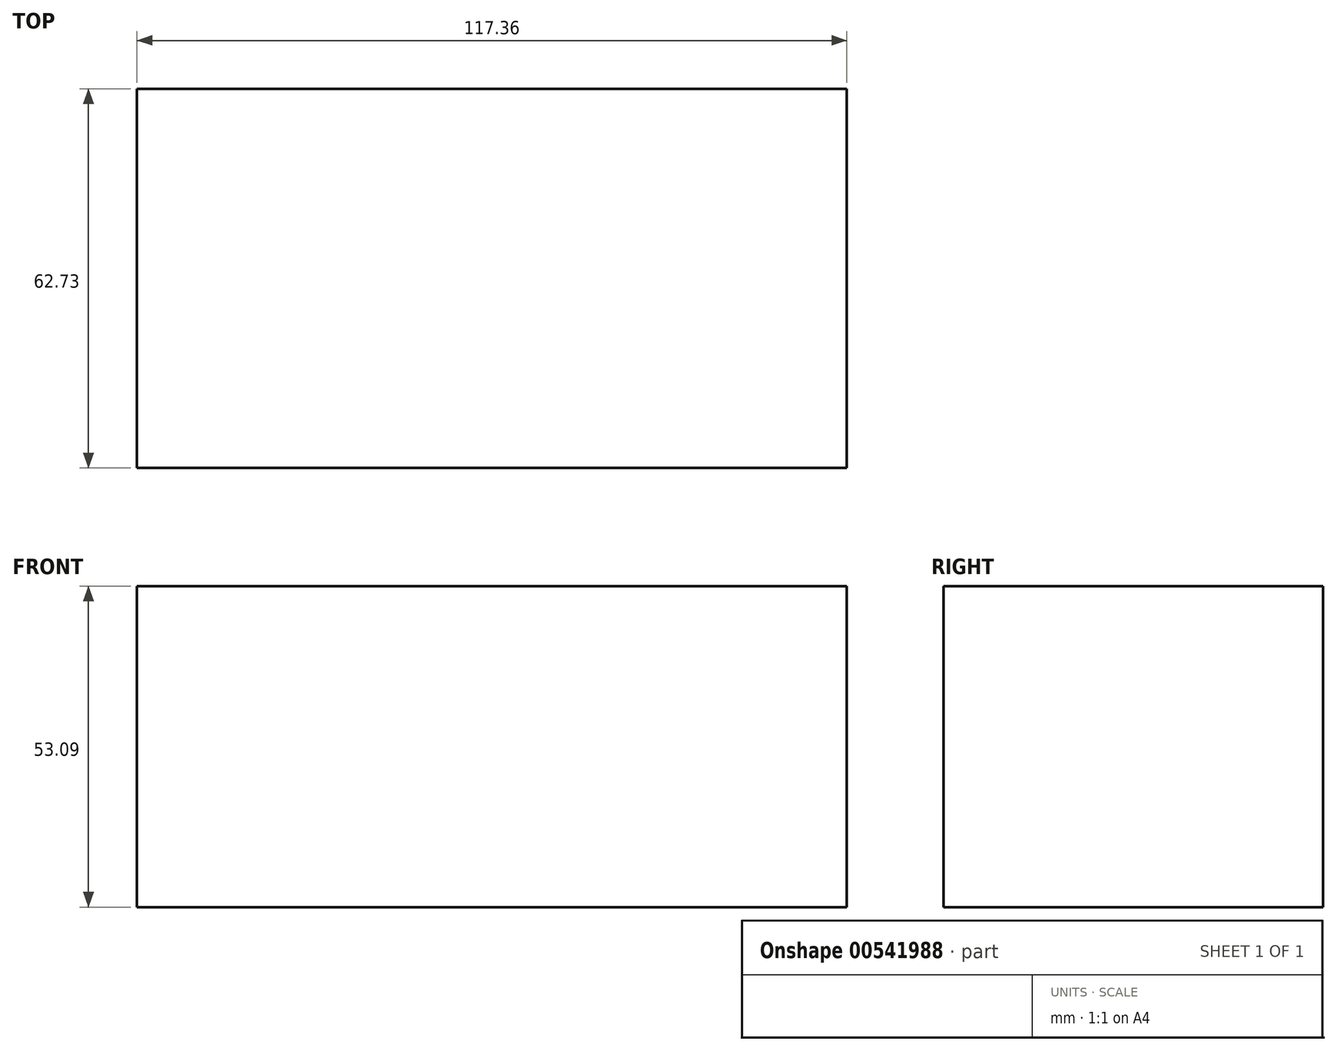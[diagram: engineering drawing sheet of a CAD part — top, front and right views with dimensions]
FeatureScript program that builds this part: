
annotation { "Feature Type Name" : "Feature", "Feature Type Description" : "" }
export const myFeature = defineFeature(function(context is Context, id is Id, definition is map)
    precondition{}
    {
        {
            var Q0;
            Q0=qCreatedBy(makeId("Top.planeOp"),FACE);
            var sketch = newSketch(context, id + "F0", { "sketchPlane" : qUnion([Q0])});
            skLineSegment(sketch, "E0.bottom", {"start": v(-122.01, 49.37) * mm, "end": v(-4.65, 49.37) * mm});
            skLineSegment(sketch, "E0.top", {"start": v(-122.01, -13.36) * mm, "end": v(-4.65, -13.36) * mm});
            skLineSegment(sketch, "E0.left", {"start": v(-122.01, 49.37) * mm, "end": v(-122.01, -13.36) * mm});
            skLineSegment(sketch, "E0.right", {"start": v(-4.65, 49.37) * mm, "end": v(-4.65, -13.36) * mm});
            skSolve(sketch);
        }
        {
            var Q0;
            Q0=makeQuery(id+"F0.imprint","IMPRINT",FACE,{"disambiguationData":[TD([[makeQuery(id+"F0.imprint","IMPRINT",EDGE,{"derivedFrom":sQuery(id+"F0.wireOp",EDGE,"E0.bottom")}),-1.0]])]});
            extrude(context, id + "F1", {"entities" : qUnion([Q0]), "depth" : 53.1 * mm, "offsetDistance" : 25.4 * mm});
        }
    });
